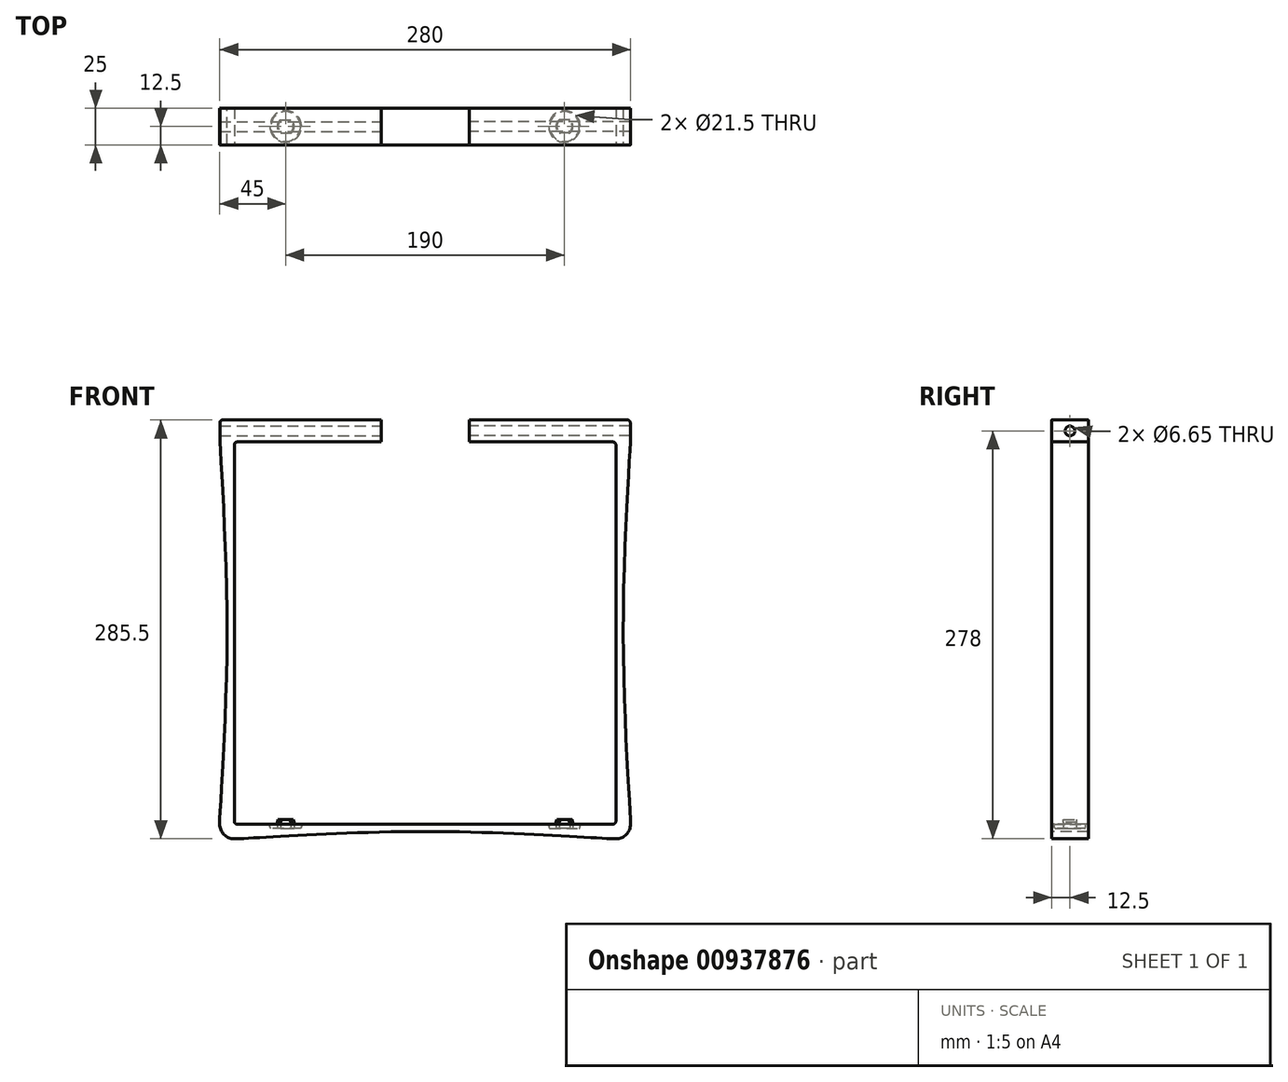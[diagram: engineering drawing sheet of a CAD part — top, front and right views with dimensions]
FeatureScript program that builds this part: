
annotation { "Feature Type Name" : "Feature", "Feature Type Description" : "" }
export const myFeature = defineFeature(function(context is Context, id is Id, definition is map)
    precondition{}
    {
        {
            var Q0;
            Q0=qCreatedBy(makeId("Front.planeOp"),FACE);
            var sketch = newSketch(context, id + "F0", { "sketchPlane" : qUnion([Q0])});
            skLineSegment(sketch, "E0.top", {"start": v(130, -132.75) * mm, "end": v(-130, -132.75) * mm});
            skLineSegment(sketch, "E0.left", {"start": v(130, 132.75) * mm, "end": v(130, -132.75) * mm});
            skLineSegment(sketch, "E0.right", {"start": v(-130, 132.75) * mm, "end": v(-130, -132.75) * mm});
            skPoint(sketch, "E0.middle", {"position": v(0, 0) * mm});
            skCircle(sketch, "E1", {"center": v(-130, 132.75) * mm, "radius": 10 * mm});
            skCircle(sketch, "E2", {"center": v(130, 132.75) * mm, "radius": 10 * mm});
            skCircle(sketch, "E3", {"center": v(-130, -132.75) * mm, "radius": 10 * mm});
            skCircle(sketch, "E4", {"center": v(130, -132.75) * mm, "radius": 10 * mm});
            skPoint(sketch, "E5", {"position": v(130, 122.75) * mm});
            skPoint(sketch, "E6", {"position": v(130, -122.75) * mm});
            skPoint(sketch, "E7", {"position": v(120, -132.75) * mm});
            skPoint(sketch, "E8", {"position": v(-120, -132.75) * mm});
            skPoint(sketch, "E9", {"position": v(-130, -122.75) * mm});
            skPoint(sketch, "E10", {"position": v(-130, 122.75) * mm});
            skPoint(sketch, "E11", {"position": v(135, 0) * mm});
            skPoint(sketch, "E12", {"position": v(0, -137.75) * mm});
            skPoint(sketch, "E13", {"position": v(-135, 0) * mm});
            skFitSpline(sketch, "E14", {"points": [v(140, 132.75) * mm, v(135, 0) * mm, v(140, -132.75) * mm], "startDerivative": vector(0, -60) * mm, "endDerivative": vector(0, -60) * mm});
            skFitSpline(sketch, "E15", {"points": [v(130, -142.75) * mm, v(0, -137.75) * mm, v(-130, -142.75) * mm], "startDerivative": vector(-60, 0) * mm, "endDerivative": vector(-60, 0) * mm});
            skFitSpline(sketch, "E16", {"points": [v(-140, 132.75) * mm, v(-135, 0) * mm, v(-140, -132.75) * mm], "startDerivative": vector(0, -60) * mm, "endDerivative": vector(0, -60) * mm});
            skLineSegment(sketch, "E17", {"start": v(0, -132.75) * mm, "end": v(0, -137.75) * mm});
            skLineSegment(sketch, "E18", {"start": v(-130, 127.75) * mm, "end": v(130, 127.75) * mm});
            skLineSegment(sketch, "E19", {"start": v(-130, 142.75) * mm, "end": v(130, 142.75) * mm});
            skLineSegment(sketch, "E20", {"start": v(-30, 142.75) * mm, "end": v(-30, 127.75) * mm});
            skPoint(sketch, "E21", {"position": v(0, 142.75) * mm});
            skLineSegment(sketch, "E22", {"start": v(-139.84, 127.75) * mm, "end": v(-139.84, 142.75) * mm});
            skLineSegment(sketch, "E23", {"start": v(-139.84, 142.75) * mm, "end": v(-130, 142.75) * mm});
            skSolve(sketch);
        }
        {
            var Q0;
            {var subQ3=sQuery(id+"F0.wireOp",EDGE,"E0.bottom");var subQ5=sQuery(id+"F0.wireOp",EDGE,"E0.right");var subQ6=makeQuery(id+"F0.imprint","INTERSECT",VERTEX,{"derivedFrom":[subQ3,subQ5]});Q0=makeQuery(id+"F0.imprint","IMPRINT",FACE,{"disambiguationData":[TD([[makeQuery(id+"F0.imprint","IMPRINT",EDGE,{"disambiguationData":[TD([[subQ6,1.0]])],"derivedFrom":subQ3}),-1.0]])]});}
            var Q1;
            {var subQ3=sQuery(id+"F0.wireOp",EDGE,"E0.right");var subQ4=sQuery(id+"F0.wireOp",EDGE,"E0.top");var subQ5=makeQuery(id+"F0.imprint","INTERSECT",VERTEX,{"derivedFrom":[subQ4,subQ3]});Q1=makeQuery(id+"F0.imprint","IMPRINT",FACE,{"disambiguationData":[TD([[makeQuery(id+"F0.imprint","IMPRINT",EDGE,{"disambiguationData":[TD([[subQ5,1.0]])],"derivedFrom":subQ4}),1.0]])]});}
            var Q2;
            {var subQ0=sQuery(id+"F0.wireOp",EDGE,"chU375EZ-pw4W-Z8qP-1X7N-BxzHXrx6lz4L");var subQ1=makeQuery(id+"F0.imprint","INTERSECT",VERTEX,{"derivedFrom":[sQuery(id+"F0.wireOp",EDGE,"E0.bottom"),sQuery(id+"F0.wireOp",EDGE,"E0.right"),subQ0]});Q2=makeQuery(id+"F0.imprint","IMPRINT",FACE,{"disambiguationData":[TD([[makeQuery(id+"F0.imprint","IMPRINT",EDGE,{"disambiguationData":[TD([[subQ1,1.0]])],"derivedFrom":subQ0}),1.0]])]});}
            var Q3;
            {var subQ0=sQuery(id+"F0.wireOp",EDGE,"ggXTJQuI-1H89-RfiE-NsBS-uQXSnbsqAiaE");Q3=makeQuery(id+"F0.imprint","IMPRINT",FACE,{"disambiguationData":[TD([[makeQuery(id+"F0.imprint","IMPRINT",EDGE,{"derivedFrom":subQ0}),1.0]])]});}
            var Q4;
            {var subQ3=sQuery(id+"F0.wireOp",EDGE,"gdohUwQN-cRY9-JMmu-iZ8n-Zr5zuHgMpPtE");Q4=makeQuery(id+"F0.imprint","IMPRINT",FACE,{"disambiguationData":[TD([[makeQuery(id+"F0.imprint","IMPRINT",EDGE,{"derivedFrom":subQ3}),-1.0]])]});}
            var Q5;
            {var subQ9=sQuery(id+"F0.wireOp",EDGE,"tLdlqTSF-1ZpZ-UICR-f0JC-3COKoblnljaa");Q5=makeQuery(id+"F0.imprint","IMPRINT",FACE,{"disambiguationData":[TD([[makeQuery(id+"F0.imprint","IMPRINT",EDGE,{"derivedFrom":subQ9}),-1.0]])]});}
            var Q6;
            {var subQ1=sQuery(id+"F0.wireOp",EDGE,"FMSI08yi-jxhI-lF5w-pUc4-U6R0Bl7jVKgF");var subQ3=sQuery(id+"F0.wireOp",EDGE,"kju9rNBw-g8C0-CVsP-cpWZ-8EKg8xuZ4Rlv");var subQ4=makeQuery(id+"F0.imprint","INTERSECT",VERTEX,{"derivedFrom":[subQ1,subQ3]});Q6=makeQuery(id+"F0.imprint","IMPRINT",FACE,{"disambiguationData":[TD([[makeQuery(id+"F0.imprint","IMPRINT",EDGE,{"disambiguationData":[TD([[subQ4,1.0]])],"derivedFrom":subQ3}),-1.0]])]});}
            var Q7;
            {var subQ1=sQuery(id+"F0.wireOp",EDGE,"2b602db3-8cde-4b4d-94c1-4e163f69051a");var subQ3=sQuery(id+"F0.wireOp",EDGE,"AlPE6Xrp-ujQs-Fq92-D5fd-AYqgaEszeJRF");var subQ4=makeQuery(id+"F0.imprint","INTERSECT",VERTEX,{"derivedFrom":[subQ1,subQ3]});Q7=makeQuery(id+"F0.imprint","IMPRINT",FACE,{"disambiguationData":[TD([[makeQuery(id+"F0.imprint","IMPRINT",EDGE,{"disambiguationData":[TD([[subQ4,1.0]])],"derivedFrom":subQ3}),1.0]])]});}
            var Q8;
            {var subQ0=sQuery(id+"F0.wireOp",EDGE,"7vUGCDw5-HdKQ-Byab-KyNl-aguf2hH3S7Ws");var subQ3=sQuery(id+"F0.wireOp",EDGE,"bnrk730L-tMXp-MxFW-M0bM-bMHQUXloFIhx");var subQ5=makeQuery(id+"F0.imprint","INTERSECT",VERTEX,{"derivedFrom":[subQ0,subQ3]});Q8=makeQuery(id+"F0.imprint","IMPRINT",FACE,{"disambiguationData":[TD([[makeQuery(id+"F0.imprint","IMPRINT",EDGE,{"disambiguationData":[TD([[subQ5,-1.0]])],"derivedFrom":subQ3}),-1.0]])]});}
            var Q9;
            {var subQ0=sQuery(id+"F0.wireOp",EDGE,"bnrk730L-tMXp-MxFW-M0bM-bMHQUXloFIhx");var subQ1=sQuery(id+"F0.wireOp",EDGE,"E0.bottom");var subQ2=makeQuery(id+"F0.imprint","INTERSECT",VERTEX,{"derivedFrom":[subQ1,subQ0]});Q9=makeQuery(id+"F0.imprint","IMPRINT",FACE,{"disambiguationData":[TD([[makeQuery(id+"F0.imprint","IMPRINT",EDGE,{"disambiguationData":[TD([[subQ2,-1.0]])],"derivedFrom":subQ1}),-1.0]])]});}
            var Q10;
            {var subQ0=sQuery(id+"F0.wireOp",EDGE,"E17");Q10=makeQuery(id+"F0.imprint","IMPRINT",FACE,{"disambiguationData":[TD([[makeQuery(id+"F0.imprint","IMPRINT",EDGE,{"derivedFrom":subQ0}),-1.0]])]});}
            var Q11;
            {var subQ3=sQuery(id+"F0.wireOp",EDGE,"E20");Q11=makeQuery(id+"F0.imprint","IMPRINT",FACE,{"disambiguationData":[TD([[makeQuery(id+"F0.imprint","IMPRINT",EDGE,{"derivedFrom":subQ3}),-1.0]])]});}
            var Q12;
            {var subQ0=sQuery(id+"F0.wireOp",EDGE,"Duk5xWOL-XEPA-Kap6-KP7T-KkaFlW0BVgg9");Q12=makeQuery(id+"F0.imprint","IMPRINT",FACE,{"disambiguationData":[TD([[makeQuery(id+"F0.imprint","IMPRINT",EDGE,{"derivedFrom":subQ0}),-1.0]])]});}
            var Q13;
            {var subQ5=sQuery(id+"F0.wireOp",EDGE,"E0.right");var subQ7=sQuery(id+"F0.wireOp",EDGE,"E1");var subQ8=makeQuery(id+"F0.imprint","INTERSECT",VERTEX,{"derivedFrom":[subQ5,subQ7]});Q13=makeQuery(id+"F0.imprint","IMPRINT",FACE,{"disambiguationData":[TD([[makeQuery(id+"F0.imprint","IMPRINT",EDGE,{"disambiguationData":[TD([[subQ8,-1.0]])],"derivedFrom":subQ5}),-1.0]])]});}
            var Q14;
            {var subQ1=sQuery(id+"F0.wireOp",EDGE,"E0.right");var subQ6=sQuery(id+"F0.wireOp",EDGE,"E18");var subQ9=makeQuery(id+"F0.imprint","INTERSECT",VERTEX,{"derivedFrom":[subQ1,subQ6]});Q14=makeQuery(id+"F0.imprint","IMPRINT",FACE,{"disambiguationData":[TD([[makeQuery(id+"F0.imprint","IMPRINT",EDGE,{"disambiguationData":[TD([[subQ9,-1.0]])],"derivedFrom":subQ1}),-1.0]])]});}
            var Q15;
            {var subQ0=sQuery(id+"F0.wireOp",EDGE,"E23");Q15=makeQuery(id+"F0.imprint","IMPRINT",FACE,{"disambiguationData":[TD([[makeQuery(id+"F0.imprint","IMPRINT",EDGE,{"derivedFrom":subQ0}),-1.0]])]});}
            extrude(context, id + "F1", {"entities" : qUnion([Q0, Q1, Q2, Q3, Q4, Q5, Q6, Q7, Q8, Q9, Q10, Q11, Q12, Q13, Q14, Q15]), "oppositeDirection" : true, "depth" : 25 * mm, "offsetDistance" : 25 * mm});
        }
        {
            var Q0;
            Q0=makeQuery(id+"F1.opExtrude","SWEPT_FACE",FACE,{"disambiguationData":[OSD([sQuery(id+"F0.wireOp",EDGE,"E0.top")])]});
            var sketch = newSketch(context, id + "F2", { "sketchPlane" : qUnion([Q0])});
            skCircle(sketch, "E24", {"center": v(-95, 12.5) * mm, "radius": 5.75 * mm});
            skPoint(sketch, "E24.centerSnap0", {"position": v(-130, 12.5) * mm});
            skCircle(sketch, "E25", {"center": v(-95, 12.5) * mm, "radius": 10.75 * mm});
            skLineSegment(sketch, "E26", {"start": v(-98.58, 8) * mm, "end": v(-91.42, 8) * mm});
            skLineSegment(sketch, "E27", {"start": v(-98.58, 17) * mm, "end": v(-91.42, 17) * mm});
            skSolve(sketch);
        }
        {
            var Q0;
            Q0=makeQuery(id+"F2.imprint","IMPRINT",FACE,{"disambiguationData":[TD([[makeQuery(id+"F2.imprint","IMPRINT",EDGE,{"derivedFrom":sQuery(id+"F2.wireOp",EDGE,"E24")}),1.0]])]});
            extrude(context, id + "F3", {"entities" : qUnion([Q0]), "operationType" : NewBodyOperationType.ADD, "depth" : 3 * mm, "offsetDistance" : 25 * mm});
        }
        {
            var Q0;
            Q0=makeQuery(id+"F2.imprint","IMPRINT",FACE,{"disambiguationData":[TD([[makeQuery(id+"F2.imprint","IMPRINT",EDGE,{"derivedFrom":sQuery(id+"F2.wireOp",EDGE,"E24")}),-1.0]])]});
            var Q1;
            {var subQ0=sQuery(id+"F2.wireOp",EDGE,"E26");Q1=makeQuery(id+"F2.imprint","IMPRINT",FACE,{"disambiguationData":[TD([[makeQuery(id+"F2.imprint","IMPRINT",EDGE,{"derivedFrom":subQ0}),-1.0]])]});}
            var Q2;
            {var subQ0=sQuery(id+"F2.wireOp",EDGE,"E27");Q2=makeQuery(id+"F2.imprint","IMPRINT",FACE,{"disambiguationData":[TD([[makeQuery(id+"F2.imprint","IMPRINT",EDGE,{"derivedFrom":subQ0}),1.0]])]});}
            extrude(context, id + "F4", {"entities" : qUnion([Q0, Q1, Q2]), "operationType" : NewBodyOperationType.REMOVE, "oppositeDirection" : true, "depth" : 3 * mm, "offsetDistance" : 25 * mm});
        }
        {
            var Q0;
            {var subQ0=sQuery(id+"F2.wireOp",EDGE,"E25");var subQ1=sQuery(id+"F0.wireOp",EDGE,"E0.top");Q0=makeQuery(id+"F4.boolean.opBoolean","COPY",EDGE,{"derivedFrom":makeQuery(id+"F4.opExtrude","CAP_EDGE",EDGE,{"disambiguationData":[OSD([subQ0]),TDD([makeQuery(id+"F2.imprint","IMPRINT",EDGE,{"disambiguationData":[TD([[makeQuery(id+"F2.imprint","INTERSECT",VERTEX,{"disambiguationData":[OD(0.0)],"derivedFrom":[makeQuery(id+"F1.opExtrude","CAP_EDGE",EDGE,{"disambiguationData":[OSD([subQ1])],"isStart":false}),subQ0]}),-1.0]])],"derivedFrom":subQ0})])],"isStart":false})});}
            var Q1;
            {var subQ0=sQuery(id+"F2.wireOp",EDGE,"E25");var subQ1=sQuery(id+"F0.wireOp",EDGE,"E0.top");Q1=makeQuery(id+"F4.boolean.opBoolean","COPY",EDGE,{"derivedFrom":makeQuery(id+"F4.opExtrude","CAP_EDGE",EDGE,{"disambiguationData":[OSD([subQ0]),TDD([makeQuery(id+"F2.imprint","IMPRINT",EDGE,{"disambiguationData":[TD([[makeQuery(id+"F2.imprint","INTERSECT",VERTEX,{"disambiguationData":[OD(1.0)],"derivedFrom":[makeQuery(id+"F1.opExtrude","CAP_EDGE",EDGE,{"disambiguationData":[OSD([subQ1])],"isStart":false}),subQ0]}),1.0]])],"derivedFrom":subQ0})])],"isStart":false})});}
            chamfer(context, id + "F5", {"entities" : qUnion([Q0, Q1]), "chamferType" : ChamferType.OFFSET_ANGLE, "width" : .6 * mm, "oppositeDirection" : false, "angle" : 60 * degree, "tangentPropagation" : true});
        }
        {
            var Q0;
            {var subQ0=sQuery(id+"F2.wireOp",EDGE,"E25");Q0=makeQuery(id+"F5.opChamfer","BLEND_EDGE",EDGE,{"blendedFrom":[makeQuery(id+"F4.boolean.opBoolean","COPY",EDGE,{"derivedFrom":makeQuery(id+"F4.opExtrude","CAP_EDGE",EDGE,{"disambiguationData":[OSD([subQ0])],"isStart":false})}),makeQuery(id+"F4.boolean.opBoolean","COPY",FACE,{"derivedFrom":makeQuery(id+"F4.opExtrude","SWEPT_FACE",FACE,{"disambiguationData":[OSD([subQ0])]})})],"blendedInto":[makeQuery(id+"F4.boolean.opBoolean","COPY",FACE,{"derivedFrom":makeQuery(id+"F4.opExtrude","SWEPT_FACE",FACE,{"disambiguationData":[OSD([subQ0])]})})]});}
            fillet(context, id + "F6", {"entities" : qUnion([Q0]), "radius" : 5 * mm, "tangentPropagation" : true, "allowEdgeOverflow" : false});
        }
        {
            var Q0;
            Q0=makeQuery(id+"F1.opExtrude","SWEPT_EDGE",EDGE,{"disambiguationData":[OSD([sQuery(id+"F0.wireOp",EDGE,"E0.top"),sQuery(id+"F0.wireOp",EDGE,"E0.right")])]});
            var Q1;
            Q1=makeQuery(id+"F1.opExtrude","SWEPT_EDGE",EDGE,{"disambiguationData":[OSD([sQuery(id+"F0.wireOp",EDGE,"E0.bottom"),sQuery(id+"F0.wireOp",EDGE,"E0.right")])]});
            var Q2;
            Q2=makeQuery(id+"F1.opExtrude","SWEPT_EDGE",EDGE,{"disambiguationData":[OSD([sQuery(id+"F0.wireOp",EDGE,"E22"),sQuery(id+"F0.wireOp",EDGE,"E23")])]});
            fillet(context, id + "F7", {"entities" : qUnion([Q0, Q1, Q2]), "radius" : 2 * mm, "tangentPropagation" : true, "defaultsChanged" : false, "vertexSettings" : [], "allowEdgeOverflow" : false});
        }
        {
            var Q0;
            Q0=makeQuery(id+"F3.opExtrude","CAP_EDGE",EDGE,{"disambiguationData":[OSD([sQuery(id+"F2.wireOp",EDGE,"E24")])],"isStart":false});
            chamfer(context, id + "F8", {"entities" : qUnion([Q0]), "chamferType" : ChamferType.OFFSET_ANGLE, "width" : .5 * mm, "oppositeDirection" : false, "angle" : 75 * degree, "tangentPropagation" : true});
        }
        {
            var Q0;
            Q0=makeQuery(id+"F1.opExtrude","SWEPT_FACE",FACE,{"disambiguationData":[OSD([sQuery(id+"F0.wireOp",EDGE,"E20")])]});
            var sketch = newSketch(context, id + "F9", { "sketchPlane" : qUnion([Q0])});
            skPoint(sketch, "E28", {"position": v(12.5, 135.25) * mm});
            skPoint(sketch, "E28.positionSnap0", {"position": v(12.5, 142.75) * mm});
            skPoint(sketch, "E28.positionSnap1", {"position": v(0, 135.25) * mm});
            skSolve(sketch);
        }
        {
            var Q0;
            Q0=sQuery(id+"F9.wireOp",VERTEX,"E28");
            var Q1;
            Q1=makeQuery(id+"F1.opExtrude","SWEPT_BODY",BODY,{"disambiguationData":[OSD([sQuery(id+"F0.wireOp",EDGE,"E0.bottom"),sQuery(id+"F0.wireOp",EDGE,"E0.top"),sQuery(id+"F0.wireOp",EDGE,"E0.right"),sQuery(id+"F0.wireOp",EDGE,"E3"),sQuery(id+"F0.wireOp",EDGE,"E15"),sQuery(id+"F0.wireOp",EDGE,"E16"),sQuery(id+"F0.wireOp",EDGE,"7vUGCDw5-HdKQ-Byab-KyNl-aguf2hH3S7Ws"),sQuery(id+"F0.wireOp",EDGE,"gdohUwQN-cRY9-JMmu-iZ8n-Zr5zuHgMpPtE"),sQuery(id+"F0.wireOp",EDGE,"bnrk730L-tMXp-MxFW-M0bM-bMHQUXloFIhx"),sQuery(id+"F0.wireOp",EDGE,"E17")])]});
            hole(context, id + "F10", {"style" : HoleStyle.SIMPLE, "endStyle" : HoleEndStyle.THROUGH, "holeDiameter" : 6.35 * mm + .3 * mm, "majorDiameter" : 5 * mm, "isTappedThrough" : true, "tappedDepth" : 12 * mm, "tapClearance" : 3, "locations" : qUnion([Q0]), "scope" : qUnion([Q1])});
        }
        {
            var Q0;
            Q0=makeQuery(id+"F1.opExtrude","SWEPT_BODY",BODY,{"disambiguationData":[OSD([sQuery(id+"F0.wireOp",EDGE,"E0.bottom"),sQuery(id+"F0.wireOp",EDGE,"E0.top"),sQuery(id+"F0.wireOp",EDGE,"E0.right"),sQuery(id+"F0.wireOp",EDGE,"E3"),sQuery(id+"F0.wireOp",EDGE,"E15"),sQuery(id+"F0.wireOp",EDGE,"E16"),sQuery(id+"F0.wireOp",EDGE,"7vUGCDw5-HdKQ-Byab-KyNl-aguf2hH3S7Ws"),sQuery(id+"F0.wireOp",EDGE,"gdohUwQN-cRY9-JMmu-iZ8n-Zr5zuHgMpPtE"),sQuery(id+"F0.wireOp",EDGE,"bnrk730L-tMXp-MxFW-M0bM-bMHQUXloFIhx"),sQuery(id+"F0.wireOp",EDGE,"E17")])]});
            var Q1;
            Q1=makeQuery(id+"F1.opExtrude","SWEPT_FACE",FACE,{"disambiguationData":[OSD([sQuery(id+"F0.wireOp",EDGE,"E17")])]});
            mirror(context, id + "F11", {"operationType" : NewBodyOperationType.ADD, "entities" : qUnion([Q0]), "mirrorPlane" : qUnion([Q1])});
        }
    });
